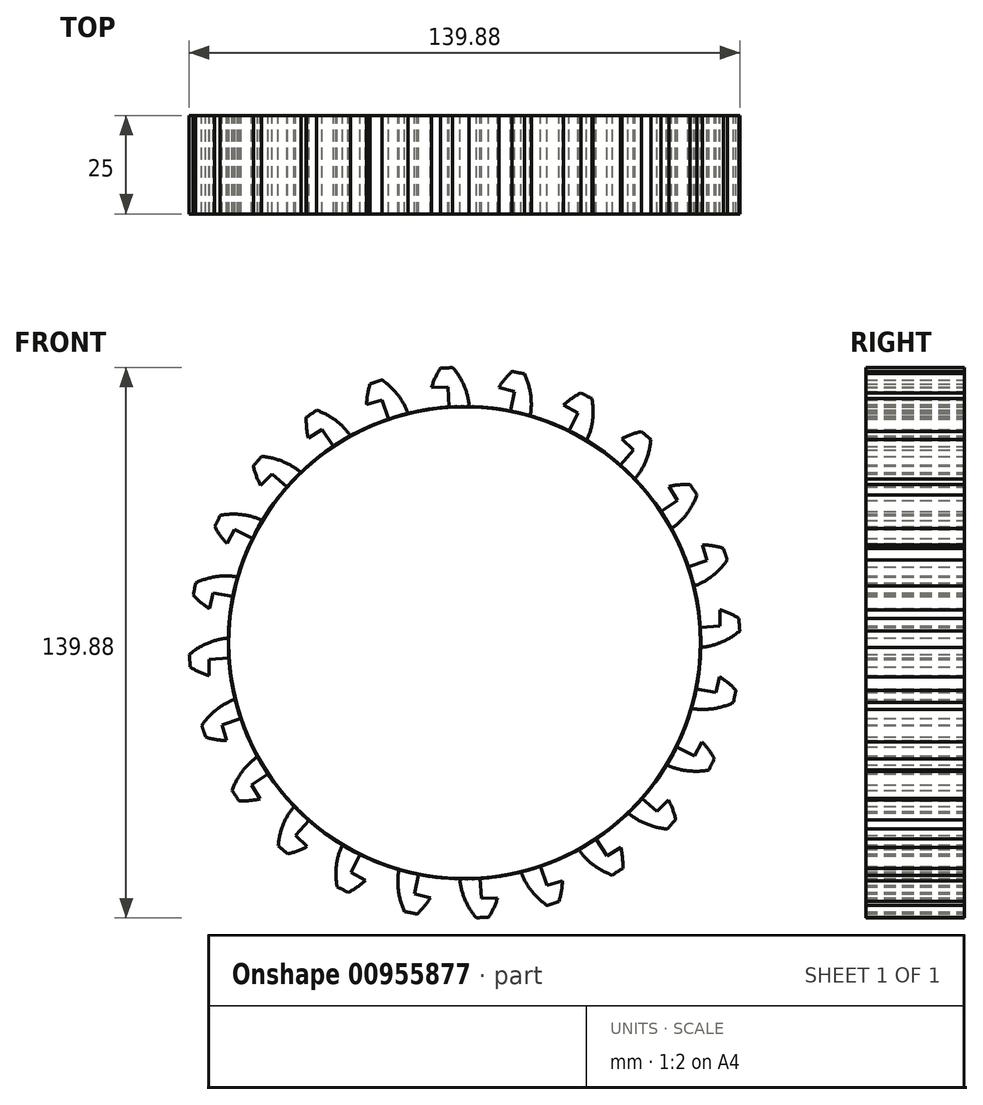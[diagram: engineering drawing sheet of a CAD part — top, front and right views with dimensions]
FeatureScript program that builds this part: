
annotation { "Feature Type Name" : "Feature", "Feature Type Description" : "" }
export const myFeature = defineFeature(function(context is Context, id is Id, definition is map)
    precondition{}
    {
        {
            var Q0;
            Q0=qCreatedBy(makeId("Front.planeOp"),FACE);
            var sketch = newSketch(context, id + "F0", { "sketchPlane" : qUnion([Q0])});
            skCircle(sketch, "E0", {"center": v(0, 0) * mm, "radius": 60 * mm});
            skCircle(sketch, "E1", {"center": v(0, 0) * mm, "radius": 65 * mm, "construction": true});
            skCircle(sketch, "E2", {"center": v(0, 0) * mm, "radius": 70 * mm, "construction": true});
            skLineSegment(sketch, "E3", {"start": v(0, 0) * mm, "end": v(0, 91.12) * mm, "construction": true});
            skLineSegment(sketch, "E4", {"start": v(0, 0) * mm, "end": v(-5.96, 91) * mm});
            skLineSegment(sketch, "E5", {"start": v(0, 65) * mm, "end": v(-58.44, 64.08) * mm});
            skLineSegment(sketch, "E6", {"start": v(0, 65) * mm, "end": v(-58.95, 42.48) * mm, "construction": true});
            skCircle(sketch, "E7", {"center": v(0, 65) * mm, "radius": 17.5 * mm, "construction": true});
            skCircle(sketch, "E8", {"center": v(0, 0) * mm, "radius": 60.72 * mm, "construction": true});
            skCircle(sketch, "E9", {"center": v(-16.24, 58.5) * mm, "radius": 17.5 * mm, "construction": true});
            skArc(sketch, "E10", {"start": v(0, 65) * mm, "mid": v(-1.3, 67.59) * mm, "end": v(-3, 69.94) * mm});
            skArc(sketch, "E11", {"start": v(1.2, 59.99) * mm, "mid": v(0.8, 62.54) * mm, "end": v(0, 65) * mm});
            skArc(sketch, "E12.MirrorCS", {"start": v(-8.48, 64.44) * mm, "mid": v(-7.52, 67.18) * mm, "end": v(-6.15, 69.73) * mm});
            skArc(sketch, "E13.MirrorCS", {"start": v(-9.01, 59.32) * mm, "mid": v(-8.95, 61.9) * mm, "end": v(-8.48, 64.44) * mm});
            skArc(sketch, "E14", {"start": v(-6.15, 69.73) * mm, "mid": v(-4.57, 69.8) * mm, "end": v(-3, 69.94) * mm});
            skSolve(sketch);
        }
        {
            var Q0;
            {var subQ0=sQuery(id+"F0.wireOp",EDGE,"E0");var subQ1=makeQuery(id+"F0.imprint","INTERSECT",VERTEX,{"derivedFrom":[subQ0,sQuery(id+"F0.wireOp",EDGE,"E11")]});Q0=makeQuery(id+"F0.imprint","IMPRINT",FACE,{"disambiguationData":[TD([[makeQuery(id+"F0.imprint","IMPRINT",EDGE,{"disambiguationData":[TD([[subQ1,-1.0]])],"derivedFrom":subQ0}),1.0]])]});}
            var Q1;
            {var subQ0=sQuery(id+"F0.wireOp",EDGE,"E13.MirrorCS");Q1=makeQuery(id+"F0.imprint","IMPRINT",FACE,{"disambiguationData":[TD([[makeQuery(id+"F0.imprint","IMPRINT",EDGE,{"derivedFrom":subQ0}),-1.0]])]});}
            var Q2;
            {var subQ0=sQuery(id+"F0.wireOp",EDGE,"E14");var subQ1=sQuery(id+"F0.wireOp",EDGE,"E4");var subQ2=makeQuery(id+"F0.imprint","INTERSECT",VERTEX,{"derivedFrom":[subQ1,subQ0]});Q2=makeQuery(id+"F0.imprint","IMPRINT",FACE,{"disambiguationData":[TD([[makeQuery(id+"F0.imprint","IMPRINT",EDGE,{"disambiguationData":[TD([[subQ2,1.0]])],"derivedFrom":subQ1}),1.0]])]});}
            var Q3;
            {var subQ5=sQuery(id+"F0.wireOp",EDGE,"E10");Q3=makeQuery(id+"F0.imprint","IMPRINT",FACE,{"disambiguationData":[TD([[makeQuery(id+"F0.imprint","IMPRINT",EDGE,{"derivedFrom":subQ5}),1.0]])]});}
            var Q4;
            {var subQ0=sQuery(id+"F0.wireOp",EDGE,"E11");Q4=makeQuery(id+"F0.imprint","IMPRINT",FACE,{"disambiguationData":[TD([[makeQuery(id+"F0.imprint","IMPRINT",EDGE,{"derivedFrom":subQ0}),1.0]])]});}
            extrude(context, id + "F1", {"entities" : qUnion([Q0, Q1, Q2, Q3, Q4]), "depth" : 25 * mm, "offsetDistance" : 25 * mm});
        }
        {
            var Q0;
            Q0=makeQuery(id+"F1.opExtrude","SWEPT_BODY",BODY,{"disambiguationData":[OSD([sQuery(id+"F0.wireOp",EDGE,"E0"),sQuery(id+"F0.wireOp",EDGE,"E10"),sQuery(id+"F0.wireOp",EDGE,"E11"),sQuery(id+"F0.wireOp",EDGE,"E12.MirrorCS"),sQuery(id+"F0.wireOp",EDGE,"E13.MirrorCS"),sQuery(id+"F0.wireOp",EDGE,"E14")])]});
            var Q1;
            Q1=makeQuery(id+"F1.opExtrude","CAP_EDGE",EDGE,{"disambiguationData":[OSD([sQuery(id+"F0.wireOp",EDGE,"E0")])],"isStart":false});
            circularPattern(context, id + "F2", {"entities" : qUnion([Q0]), "axis" : qUnion([Q1]), "angle" : 15 * degree, "instanceCount" : 24, "oppositeDirection" : true});
        }
    });
